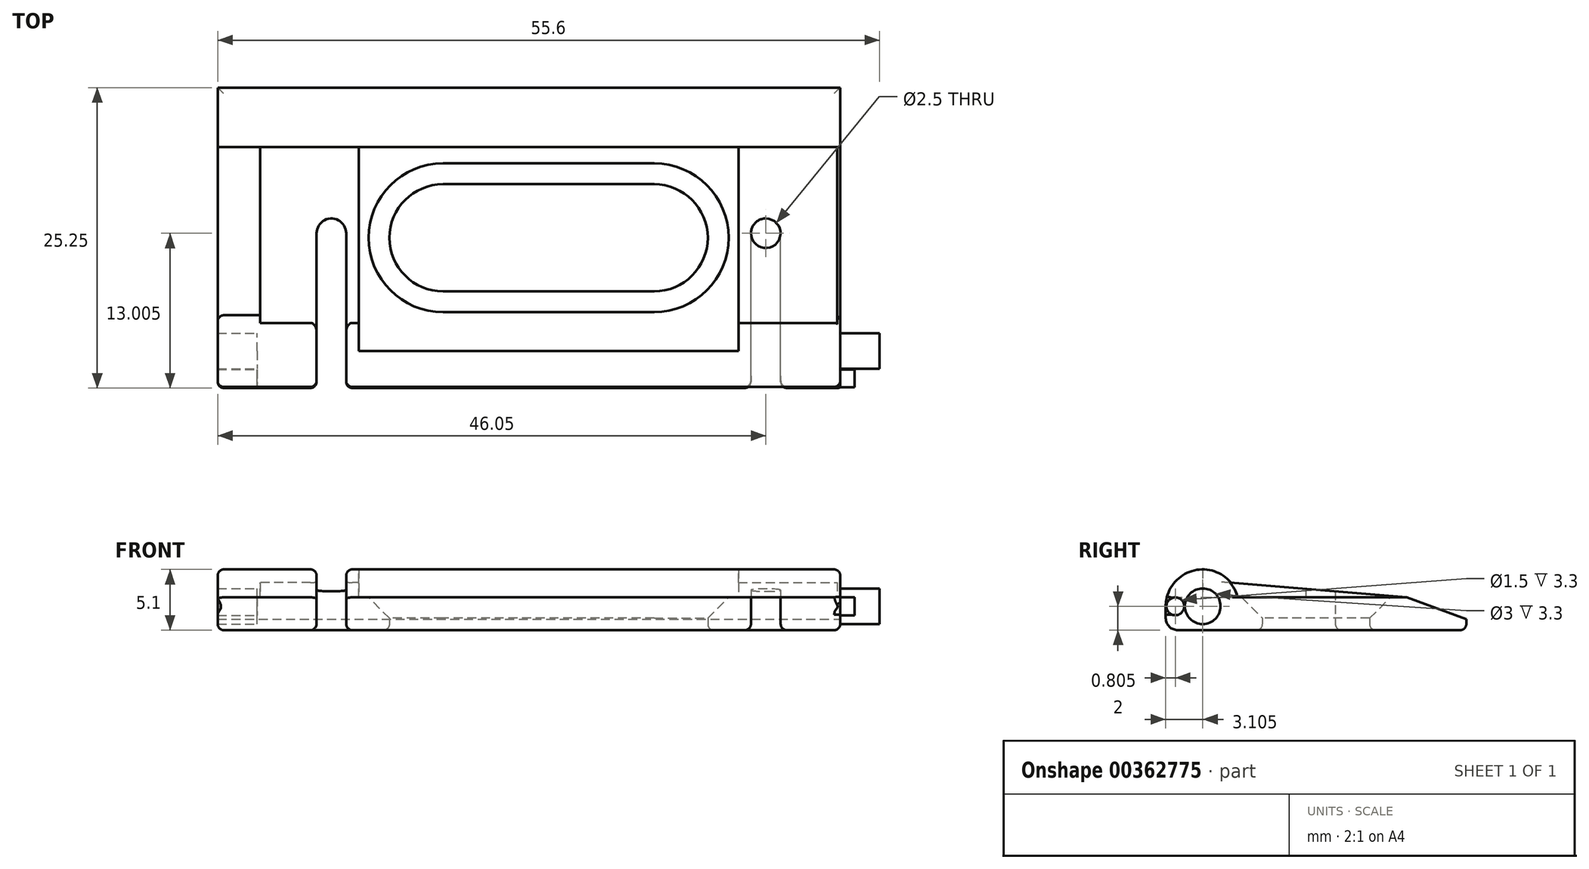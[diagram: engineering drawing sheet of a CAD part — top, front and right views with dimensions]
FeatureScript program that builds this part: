
annotation { "Feature Type Name" : "Feature", "Feature Type Description" : "" }
export const myFeature = defineFeature(function(context is Context, id is Id, definition is map)
    precondition{}
    {
        {
            var Q0;
            Q0=qCreatedBy(makeId("Top.planeOp"),FACE);
            var sketch = newSketch(context, id + "F0", { "sketchPlane" : qUnion([Q0])});
            skLineSegment(sketch, "E0.bottom", {"start": v(24.5, -12.62) * mm, "end": v(-24.5, -12.63) * mm});
            skLineSegment(sketch, "E0.top", {"start": v(24.5, 12.63) * mm, "end": v(-24.5, 12.62) * mm});
            skLineSegment(sketch, "E0.left", {"start": v(24.5, -12.62) * mm, "end": v(24.5, 12.63) * mm});
            skLineSegment(sketch, "E0.right", {"start": v(-24.5, -12.62) * mm, "end": v(-24.5, 12.62) * mm});
            skPoint(sketch, "E0.middle", {"position": v(0, 0) * mm});
            skLineSegment(sketch, "E1.bottom", {"start": v(8.88, -4.5) * mm, "end": v(-8.88, -4.5) * mm});
            skLineSegment(sketch, "E1.top", {"start": v(8.88, 4.5) * mm, "end": v(-8.88, 4.5) * mm});
            skLineSegment(sketch, "E1.left", {"start": v(8.88, -4.5) * mm, "end": v(8.88, 4.5) * mm});
            skLineSegment(sketch, "E1.right", {"start": v(-8.88, -4.5) * mm, "end": v(-8.88, 4.5) * mm});
            skCircle(sketch, "E2", {"center": v(-8.88, 0) * mm, "radius": 4.5 * mm});
            skCircle(sketch, "E3", {"center": v(8.88, 0) * mm, "radius": 4.5 * mm});
            skLineSegment(sketch, "E4", {"start": v(24.5, -12.62) * mm, "end": v(19.5, -12.62) * mm, "construction": true});
            skLineSegment(sketch, "E5.bottom", {"start": v(19.5, -12.62) * mm, "end": v(17, -12.62) * mm});
            skLineSegment(sketch, "E5.top", {"start": v(19.5, 0.38) * mm, "end": v(17, 0.38) * mm});
            skLineSegment(sketch, "E5.left", {"start": v(19.5, -12.62) * mm, "end": v(19.5, 0.38) * mm});
            skLineSegment(sketch, "E5.right", {"start": v(17, -12.62) * mm, "end": v(17, 0.38) * mm});
            skLineSegment(sketch, "E6.MirrorCS", {"start": v(-19.5, -12.62) * mm, "end": v(-19.5, 0.38) * mm});
            skLineSegment(sketch, "E7.MirrorCS", {"start": v(-17, -12.62) * mm, "end": v(-17, 0.38) * mm});
            skLineSegment(sketch, "E8.MirrorCS", {"start": v(-19.5, 0.38) * mm, "end": v(-17, 0.38) * mm});
            skLineSegment(sketch, "E9.MirrorCS", {"start": v(-19.5, -12.62) * mm, "end": v(-17, -12.62) * mm});
            skCircle(sketch, "E10", {"center": v(18.25, 0.38) * mm, "radius": 1.25 * mm});
            skCircle(sketch, "E11", {"center": v(-18.25, 0.38) * mm, "radius": 1.25 * mm});
            skSolve(sketch);
        }
        {
            var Q0;
            Q0=makeQuery(id+"F0.imprint","IMPRINT",FACE,{"disambiguationData":[TD([[makeQuery(id+"F0.imprint","IMPRINT",EDGE,{"derivedFrom":sQuery(id+"F0.wireOp",EDGE,"E0.bottom")}),-1.0]])]});
            extrude(context, id + "F1", {"entities" : qUnion([Q0]), "depth" : 2.75 * mm});
        }
        {
            var Q0;
            Q0=makeQuery(id+"F1.opExtrude","CAP_EDGE",EDGE,{"disambiguationData":[OSD([sQuery(id+"F0.wireOp",EDGE,"E2")])],"isStart":false});
            var Q1;
            Q1=makeQuery(id+"F1.opExtrude","CAP_EDGE",EDGE,{"disambiguationData":[OSD([sQuery(id+"F0.wireOp",EDGE,"E1.top")])],"isStart":false});
            var Q2;
            Q2=makeQuery(id+"F1.opExtrude","CAP_EDGE",EDGE,{"disambiguationData":[OSD([sQuery(id+"F0.wireOp",EDGE,"E3")])],"isStart":false});
            var Q3;
            Q3=makeQuery(id+"F1.opExtrude","CAP_EDGE",EDGE,{"disambiguationData":[OSD([sQuery(id+"F0.wireOp",EDGE,"E1.bottom")])],"isStart":false});
            chamfer(context, id + "F2", {"entities" : qUnion([Q0, Q1, Q2, Q3]), "width" : 1.75 * mm, "tangentPropagation" : true});
        }
        {
            var Q0;
            Q0=makeQuery(id+"F1.opExtrude","CAP_EDGE",EDGE,{"disambiguationData":[OSD([sQuery(id+"F0.wireOp",EDGE,"E1.bottom")])],"isStart":true});
            var Q1;
            Q1=makeQuery(id+"F1.opExtrude","CAP_EDGE",EDGE,{"disambiguationData":[OSD([sQuery(id+"F0.wireOp",EDGE,"E3")])],"isStart":true});
            var Q2;
            Q2=makeQuery(id+"F1.opExtrude","CAP_EDGE",EDGE,{"disambiguationData":[OSD([sQuery(id+"F0.wireOp",EDGE,"E1.top")])],"isStart":true});
            var Q3;
            Q3=makeQuery(id+"F1.opExtrude","CAP_EDGE",EDGE,{"disambiguationData":[OSD([sQuery(id+"F0.wireOp",EDGE,"E2")])],"isStart":true});
            fillet(context, id + "F3", {"entities" : qUnion([Q0, Q1, Q2, Q3]), "radius" : 0.5 * mm, "tangentPropagation" : true, "allowEdgeOverflow" : false});
        }
        {
            var Q0;
            Q0=makeQuery(id+"F1.opExtrude","CAP_EDGE",EDGE,{"disambiguationData":[OSD([sQuery(id+"F0.wireOp",EDGE,"E0.top")])],"isStart":false});
            chamfer(context, id + "F4", {"entities" : qUnion([Q0]), "chamferType" : ChamferType.OFFSET_ANGLE, "width" : 5 * mm, "oppositeDirection" : false, "angle" : 20 * degree, "tangentPropagation" : true});
        }
        {
            var Q0;
            Q0=makeQuery(id+"F1.opExtrude","SWEPT_FACE",FACE,{"disambiguationData":[OSD([sQuery(id+"F0.wireOp",EDGE,"E0.left")])]});
            var sketch = newSketch(context, id + "F5", { "sketchPlane" : qUnion([Q0])});
            skLineSegment(sketch, "E12.bottom", {"start": v(-12.62, 0) * mm, "end": v(-9.53, 0) * mm, "construction": true});
            skLineSegment(sketch, "E12.top", {"start": v(-12.62, 2) * mm, "end": v(-9.53, 2) * mm, "construction": true});
            skLineSegment(sketch, "E12.left", {"start": v(-12.62, 0) * mm, "end": v(-12.62, 2) * mm, "construction": true});
            skLineSegment(sketch, "E12.right", {"start": v(-9.53, 0) * mm, "end": v(-9.53, 2) * mm, "construction": true});
            skCircle(sketch, "E13", {"center": v(-9.53, 2) * mm, "radius": 3.1 * mm});
            skPoint(sketch, "E14", {"position": v(-7.16, 4) * mm});
            skLineSegment(sketch, "E15", {"start": v(-7.16, 4) * mm, "end": v(7.63, 2.75) * mm});
            skCircle(sketch, "E16", {"center": v(-9.53, 2) * mm, "radius": 1.5 * mm});
            skCircle(sketch, "E17", {"center": v(-11.83, 2) * mm, "radius": 0.75 * mm});
            skSolve(sketch);
        }
        {
            var Q0;
            {var subQ0=sQuery(id+"F5.wireOp",EDGE,"E13");var subQ1=makeQuery(id+"F1.opExtrude","CAP_EDGE",EDGE,{"disambiguationData":[OSD([sQuery(id+"F0.wireOp",EDGE,"E0.left")])],"isStart":false});var subQ2=makeQuery(id+"F5.imprint","INTERSECT",VERTEX,{"disambiguationData":[OD(0.0)],"derivedFrom":[subQ1,subQ0]});Q0=makeQuery(id+"F5.imprint","IMPRINT",FACE,{"disambiguationData":[TD([[makeQuery(id+"F5.imprint","IMPRINT",EDGE,{"disambiguationData":[TD([[subQ2,1.0]])],"derivedFrom":subQ0}),1.0]])]});}
            var Q1;
            {var subQ0=sQuery(id+"F5.wireOp",EDGE,"E16");var subQ1=makeQuery(id+"F1.opExtrude","CAP_EDGE",EDGE,{"disambiguationData":[OSD([sQuery(id+"F0.wireOp",EDGE,"E0.left")])],"isStart":false});var subQ2=makeQuery(id+"F5.imprint","INTERSECT",VERTEX,{"disambiguationData":[OD(0.0)],"derivedFrom":[subQ1,subQ0]});Q1=makeQuery(id+"F5.imprint","IMPRINT",FACE,{"disambiguationData":[TD([[makeQuery(id+"F5.imprint","IMPRINT",EDGE,{"disambiguationData":[TD([[subQ2,1.0]])],"derivedFrom":subQ0}),1.0]])]});}
            var Q2;
            Q2=makeQuery(id+"F1.opExtrude","SWEPT_FACE",FACE,{"disambiguationData":[OSD([sQuery(id+"F0.wireOp",EDGE,"E0.right")])]});
            extrude(context, id + "F6", {"entities" : qUnion([Q0, Q1]), "operationType" : NewBodyOperationType.ADD, "endBound" : BoundingType.UP_TO_SURFACE, "oppositeDirection" : true, "endBoundEntityFace" : qUnion([Q2]), "depth" : 25 * mm});
        }
        {
            var Q0;
            {var subQ0=sQuery(id+"F0.wireOp",EDGE,"E0.bottom");Q0=makeQuery(id+"F1.opExtrude","CAP_EDGE",EDGE,{"disambiguationData":[OSD([subQ0]),TDD([makeQuery(id+"F0.imprint","IMPRINT",EDGE,{"disambiguationData":[TD([[makeQuery(id+"F0.imprint","INTERSECT",VERTEX,{"derivedFrom":[subQ0,sQuery(id+"F0.wireOp",EDGE,"E0.left")]}),-1.0]])],"derivedFrom":subQ0})])],"isStart":false});}
            var Q1;
            {var subQ0=sQuery(id+"F0.wireOp",EDGE,"E0.bottom");Q1=makeQuery(id+"F1.opExtrude","CAP_EDGE",EDGE,{"disambiguationData":[OSD([subQ0]),TDD([makeQuery(id+"F0.imprint","IMPRINT",EDGE,{"disambiguationData":[TD([[makeQuery(id+"F0.imprint","INTERSECT",VERTEX,{"derivedFrom":[subQ0,sQuery(id+"F0.wireOp",EDGE,"E5.bottom"),sQuery(id+"F0.wireOp",EDGE,"E5.right")]}),-1.0]])],"derivedFrom":subQ0})])],"isStart":false});}
            var Q2;
            {var subQ0=sQuery(id+"F0.wireOp",EDGE,"E0.bottom");Q2=makeQuery(id+"F1.opExtrude","CAP_EDGE",EDGE,{"disambiguationData":[OSD([subQ0]),TDD([makeQuery(id+"F0.imprint","IMPRINT",EDGE,{"disambiguationData":[TD([[makeQuery(id+"F0.imprint","INTERSECT",VERTEX,{"derivedFrom":[subQ0,sQuery(id+"F0.wireOp",EDGE,"E0.right")]}),1.0]])],"derivedFrom":subQ0})])],"isStart":false});}
            fillet(context, id + "F7", {"entities" : qUnion([Q0, Q1, Q2]), "radius" : 2 * mm, "tangentPropagation" : true, "allowEdgeOverflow" : false});
        }
        {
            var Q0;
            {var subQ0=sQuery(id+"F0.wireOp",EDGE,"E0.bottom");Q0=makeQuery(id+"F1.opExtrude","CAP_EDGE",EDGE,{"disambiguationData":[OSD([subQ0]),TDD([makeQuery(id+"F0.imprint","IMPRINT",EDGE,{"disambiguationData":[TD([[makeQuery(id+"F0.imprint","INTERSECT",VERTEX,{"derivedFrom":[subQ0,sQuery(id+"F0.wireOp",EDGE,"E0.right")]}),1.0]])],"derivedFrom":subQ0})])],"isStart":true});}
            var Q1;
            {var subQ0=sQuery(id+"F0.wireOp",EDGE,"E0.bottom");Q1=makeQuery(id+"F1.opExtrude","CAP_EDGE",EDGE,{"disambiguationData":[OSD([subQ0]),TDD([makeQuery(id+"F0.imprint","IMPRINT",EDGE,{"disambiguationData":[TD([[makeQuery(id+"F0.imprint","INTERSECT",VERTEX,{"derivedFrom":[subQ0,sQuery(id+"F0.wireOp",EDGE,"E5.bottom"),sQuery(id+"F0.wireOp",EDGE,"E5.right")]}),-1.0]])],"derivedFrom":subQ0})])],"isStart":true});}
            var Q2;
            {var subQ0=sQuery(id+"F0.wireOp",EDGE,"E0.bottom");Q2=makeQuery(id+"F1.opExtrude","CAP_EDGE",EDGE,{"disambiguationData":[OSD([subQ0]),TDD([makeQuery(id+"F0.imprint","IMPRINT",EDGE,{"disambiguationData":[TD([[makeQuery(id+"F0.imprint","INTERSECT",VERTEX,{"derivedFrom":[subQ0,sQuery(id+"F0.wireOp",EDGE,"E0.left")]}),-1.0]])],"derivedFrom":subQ0})])],"isStart":true});}
            fillet(context, id + "F8", {"entities" : qUnion([Q0, Q1, Q2]), "radius" : 1 * mm, "tangentPropagation" : true, "allowEdgeOverflow" : false});
        }
        {
            var Q0;
            {var subQ0=sQuery(id+"F5.wireOp",EDGE,"E15");Q0=makeQuery(id+"F5.imprint","IMPRINT",FACE,{"disambiguationData":[TD([[makeQuery(id+"F5.imprint","IMPRINT",EDGE,{"derivedFrom":subQ0}),-1.0]])]});}
            extrude(context, id + "F9", {"entities" : qUnion([Q0]), "operationType" : NewBodyOperationType.ADD, "oppositeDirection" : true, "depth" : 8.55 * mm});
        }
        {
            var Q0;
            {var subQ0=sQuery(id+"F5.wireOp",EDGE,"E15");Q0=makeQuery(id+"F5.imprint","IMPRINT",FACE,{"disambiguationData":[TD([[makeQuery(id+"F5.imprint","IMPRINT",EDGE,{"derivedFrom":subQ0}),-1.0]])]});}
            extrude(context, id + "F10", {"entities" : qUnion([Q0]), "operationType" : NewBodyOperationType.REMOVE, "oppositeDirection" : true, "depth" : 0.25 * mm});
        }
        {
            var Q0;
            {var subQ0=sQuery(id+"F0.wireOp",EDGE,"E0.right");Q0=makeQuery(id+"F6.boolean.opBoolean","MERGE",FACE,{"derivedFrom":[makeQuery(id+"F1.opExtrude","SWEPT_FACE",FACE,{"disambiguationData":[OSD([subQ0])]}),makeQuery(id+"F6.opExtrude","CAP_FACE",FACE,{"disambiguationData":[OSD([subQ0])],"isStart":false})]});}
            var sketch = newSketch(context, id + "F11", { "sketchPlane" : qUnion([Q0])});
            skArc(sketch, "E18.0.0", {"start": v(7.16, 4) * mm, "mid": v(6.77, 3.41) * mm, "end": v(6.52, 2.75) * mm});
            skLineSegment(sketch, "E18.0.1", {"start": v(6.52, 2.75) * mm, "end": v(-7.63, 2.75) * mm});
            skLineSegment(sketch, "E18.0.2", {"start": v(-7.63, 2.75) * mm, "end": v(7.16, 4) * mm});
            skSolve(sketch);
        }
        {
            var Q0;
            Q0=makeQuery(id+"F11.imprint","IMPRINT",FACE,{"disambiguationData":[TD([[makeQuery(id+"F11.imprint","IMPRINT",EDGE,{"derivedFrom":sQuery(id+"F11.wireOp",EDGE,"E18.0.0")}),1.0]])]});
            extrude(context, id + "F12", {"entities" : qUnion([Q0]), "operationType" : NewBodyOperationType.ADD, "oppositeDirection" : true, "depth" : 8.55 * mm});
        }
        {
            var Q0;
            Q0=makeQuery(id+"F11.imprint","IMPRINT",FACE,{"disambiguationData":[TD([[makeQuery(id+"F11.imprint","IMPRINT",EDGE,{"derivedFrom":sQuery(id+"F11.wireOp",EDGE,"E18.0.0")}),1.0]])]});
            extrude(context, id + "F13", {"entities" : qUnion([Q0]), "operationType" : NewBodyOperationType.REMOVE, "oppositeDirection" : true, "depth" : 0.25 * mm});
        }
        {
            var Q0;
            {var subQ0=sQuery(id+"F0.wireOp",EDGE,"E6.MirrorCS");Q0=makeQuery(id+"F0.imprint","IMPRINT",FACE,{"disambiguationData":[TD([[makeQuery(id+"F0.imprint","IMPRINT",EDGE,{"derivedFrom":subQ0}),-1.0]])]});}
            var Q1;
            Q1=makeQuery(id+"F0.imprint","IMPRINT",FACE,{"disambiguationData":[TD([[makeQuery(id+"F0.imprint","IMPRINT",EDGE,{"derivedFrom":sQuery(id+"F0.wireOp",EDGE,"E5.bottom")}),-1.0]])]});
            var Q2;
            {var subQ0=sQuery(id+"F0.wireOp",EDGE,"E5.top");Q2=makeQuery(id+"F0.imprint","IMPRINT",FACE,{"disambiguationData":[TD([[makeQuery(id+"F0.imprint","IMPRINT",EDGE,{"derivedFrom":subQ0}),-1.0]])]});}
            var Q3;
            {var subQ0=sQuery(id+"F0.wireOp",EDGE,"E5.top");Q3=makeQuery(id+"F0.imprint","IMPRINT",FACE,{"disambiguationData":[TD([[makeQuery(id+"F0.imprint","IMPRINT",EDGE,{"derivedFrom":subQ0}),1.0]])]});}
            var Q4;
            {var subQ0=sQuery(id+"F0.wireOp",EDGE,"E8.MirrorCS");Q4=makeQuery(id+"F0.imprint","IMPRINT",FACE,{"disambiguationData":[TD([[makeQuery(id+"F0.imprint","IMPRINT",EDGE,{"derivedFrom":subQ0}),-1.0]])]});}
            var Q5;
            {var subQ0=sQuery(id+"F0.wireOp",EDGE,"E8.MirrorCS");Q5=makeQuery(id+"F0.imprint","IMPRINT",FACE,{"disambiguationData":[TD([[makeQuery(id+"F0.imprint","IMPRINT",EDGE,{"derivedFrom":subQ0}),1.0]])]});}
            extrude(context, id + "F14", {"entities" : qUnion([Q0, Q1, Q2, Q3, Q4, Q5]), "operationType" : NewBodyOperationType.REMOVE, "depth" : 6 * mm});
        }
        {
            var Q0;
            {var subQ0=sQuery(id+"F0.wireOp",EDGE,"E1.top");var subQ2=sQuery(id+"F0.wireOp",EDGE,"E0.left");var subQ3=sQuery(id+"F0.wireOp",EDGE,"E10");var subQ4=sQuery(id+"F0.wireOp",EDGE,"E1.bottom");var subQ5=sQuery(id+"F0.wireOp",EDGE,"E7.MirrorCS");var subQ6=sQuery(id+"F0.wireOp",EDGE,"E6.MirrorCS");var subQ7=sQuery(id+"F0.wireOp",EDGE,"E11");var subQ8=sQuery(id+"F0.wireOp",EDGE,"E0.right");var subQ9=sQuery(id+"F0.wireOp",EDGE,"E5.left");var subQ10=sQuery(id+"F0.wireOp",EDGE,"E3");var subQ11=sQuery(id+"F0.wireOp",EDGE,"E5.right");var subQ12=sQuery(id+"F0.wireOp",EDGE,"E2");var subQ13=sQuery(id+"F0.wireOp",EDGE,"E0.top");Q0=makeQuery(id+"F6.boolean.opBoolean","SPLIT",FACE,{"disambiguationData":[TD([makeQuery(id+"F1.opExtrude","SWEPT_FACE",FACE,{"disambiguationData":[OSD([subQ3])]})])],"derivedFrom":makeQuery(id+"F1.opExtrude","CAP_FACE",FACE,{"disambiguationData":[OSD([sQuery(id+"F0.wireOp",EDGE,"E0.bottom"),subQ13,subQ2,subQ8,subQ4,subQ0,subQ12,subQ10,subQ9,subQ11,subQ6,subQ5,subQ3,subQ7])],"isStart":false})});}
            var sketch = newSketch(context, id + "F15", { "sketchPlane" : qUnion([Q0])});
            skLineSegment(sketch, "E19.0", {"start": v(15.95, -7.16) * mm, "end": v(15.95, 7.63) * mm, "construction": true});
            skLineSegment(sketch, "E20.0", {"start": v(-15.95, 7.63) * mm, "end": v(-15.95, -7.16) * mm, "construction": true});
            skLineSegment(sketch, "E21.0", {"start": v(-17, -12.53) * mm, "end": v(17, -12.53) * mm, "construction": true});
            skLineSegment(sketch, "E21.1", {"start": v(-15.95, -6.52) * mm, "end": v(15.95, -6.52) * mm, "construction": true});
            skLineSegment(sketch, "E22", {"start": v(15.95, -6.52) * mm, "end": v(15.95, -12.53) * mm});
            skLineSegment(sketch, "E23", {"start": v(-15.95, -6.52) * mm, "end": v(-15.95, -12.53) * mm});
            skPoint(sketch, "E24", {"position": v(15.95, -9.52) * mm});
            skPoint(sketch, "E25", {"position": v(-15.95, -9.53) * mm});
            skLineSegment(sketch, "E26", {"start": v(15.95, -9.52) * mm, "end": v(-15.95, -9.53) * mm});
            skLineSegment(sketch, "E27", {"start": v(-15.95, -6.52) * mm, "end": v(15.95, -6.52) * mm});
            skSolve(sketch);
        }
        {
            var Q0;
            {var subQ2=sQuery(id+"F15.wireOp",EDGE,"E26");Q0=makeQuery(id+"F15.imprint","IMPRINT",FACE,{"disambiguationData":[TD([[makeQuery(id+"F15.imprint","IMPRINT",EDGE,{"derivedFrom":subQ2}),-1.0]])]});}
            extrude(context, id + "F16", {"entities" : qUnion([Q0]), "operationType" : NewBodyOperationType.REMOVE, "depth" : 5 * mm});
        }
        {
            var Q0;
            Q0=makeQuery(id+"F5.imprint","IMPRINT",FACE,{"disambiguationData":[TD([[makeQuery(id+"F5.imprint","IMPRINT",EDGE,{"derivedFrom":sQuery(id+"F5.wireOp",EDGE,"E17")}),1.0]])]});
            extrude(context, id + "F17", {"entities" : qUnion([Q0]), "operationType" : NewBodyOperationType.ADD, "depth" : 1.2 * mm});
        }
        {
            var Q0;
            {var subQ0=sQuery(id+"F5.wireOp",EDGE,"E16");var subQ1=makeQuery(id+"F1.opExtrude","CAP_EDGE",EDGE,{"disambiguationData":[OSD([sQuery(id+"F0.wireOp",EDGE,"E0.left")])],"isStart":false});var subQ2=makeQuery(id+"F5.imprint","INTERSECT",VERTEX,{"disambiguationData":[OD(0.0)],"derivedFrom":[subQ1,subQ0]});Q0=makeQuery(id+"F5.imprint","IMPRINT",FACE,{"disambiguationData":[TD([[makeQuery(id+"F5.imprint","IMPRINT",EDGE,{"disambiguationData":[TD([[subQ2,1.0]])],"derivedFrom":subQ0}),1.0]])]});}
            var Q1;
            {var subQ0=sQuery(id+"F5.wireOp",EDGE,"E16");var subQ1=makeQuery(id+"F1.opExtrude","CAP_EDGE",EDGE,{"disambiguationData":[OSD([sQuery(id+"F0.wireOp",EDGE,"E0.left")])],"isStart":false});var subQ2=makeQuery(id+"F5.imprint","INTERSECT",VERTEX,{"disambiguationData":[OD(0.0)],"derivedFrom":[subQ1,subQ0]});Q1=makeQuery(id+"F5.imprint","IMPRINT",FACE,{"disambiguationData":[TD([[makeQuery(id+"F5.imprint","IMPRINT",EDGE,{"disambiguationData":[TD([[subQ2,-1.0]])],"derivedFrom":subQ0}),1.0]])]});}
            var Q2;
            Q2=sQuery(id+"F5.wireOp",EDGE,"E16");
            extrude(context, id + "F18", {"entities" : qUnion([Q0, Q1]), "operationType" : NewBodyOperationType.ADD, "surfaceEntities" : qUnion([Q2]), "depth" : 3.3 * mm});
        }
        {
            var Q0;
            {var subQ3=sQuery(id+"F11.wireOp",EDGE,"E18.0.0");Q0=makeQuery(id+"F11.imprint","IMPRINT",FACE,{"disambiguationData":[TD([[makeQuery(id+"F11.imprint","IMPRINT",EDGE,{"derivedFrom":subQ3}),-1.0]])]});}
            var sketch = newSketch(context, id + "F19", { "sketchPlane" : qUnion([Q0])});
            skCircle(sketch, "E28.0", {"center": v(9.52, 2) * mm, "radius": 1.5 * mm});
            skCircle(sketch, "E29.0", {"center": v(11.82, 2) * mm, "radius": 0.75 * mm});
            skSolve(sketch);
        }
        {
            var Q0;
            Q0=makeQuery(id+"F19.imprint","IMPRINT",FACE,{"disambiguationData":[TD([[makeQuery(id+"F19.imprint","IMPRINT",EDGE,{"derivedFrom":sQuery(id+"F19.wireOp",EDGE,"E28.0")}),-1.0]])]});
            extrude(context, id + "F20", {"entities" : qUnion([Q0]), "operationType" : NewBodyOperationType.ADD, "depth" : 3.3 * mm});
        }
        {
            var Q0;
            Q0=makeQuery(id+"F19.imprint","IMPRINT",FACE,{"disambiguationData":[TD([[makeQuery(id+"F19.imprint","IMPRINT",EDGE,{"derivedFrom":sQuery(id+"F19.wireOp",EDGE,"E29.0")}),-1.0]])]});
            var Q1;
            Q1=sQuery(id+"F19.wireOp",EDGE,"E29.0");
            extrude(context, id + "F21", {"entities" : qUnion([Q0]), "operationType" : NewBodyOperationType.ADD, "surfaceEntities" : qUnion([Q1]), "depth" : 1.2 * mm});
        }
        {
            var Q0;
            Q0=makeQuery(id+"F1.opExtrude","CAP_FACE",FACE,{"disambiguationData":[OSD([sQuery(id+"F0.wireOp",EDGE,"E0.bottom"),sQuery(id+"F0.wireOp",EDGE,"E0.top"),sQuery(id+"F0.wireOp",EDGE,"E0.left"),sQuery(id+"F0.wireOp",EDGE,"E0.right"),sQuery(id+"F0.wireOp",EDGE,"E1.bottom"),sQuery(id+"F0.wireOp",EDGE,"E1.top"),sQuery(id+"F0.wireOp",EDGE,"E2"),sQuery(id+"F0.wireOp",EDGE,"E3"),sQuery(id+"F0.wireOp",EDGE,"E5.left"),sQuery(id+"F0.wireOp",EDGE,"E5.right"),sQuery(id+"F0.wireOp",EDGE,"E6.MirrorCS"),sQuery(id+"F0.wireOp",EDGE,"E7.MirrorCS"),sQuery(id+"F0.wireOp",EDGE,"E10"),sQuery(id+"F0.wireOp",EDGE,"E11")])],"isStart":true});
            fillet(context, id + "F22", {"entities" : qUnion([Q0]), "radius" : 0.5 * mm, "tangentPropagation" : true, "allowEdgeOverflow" : false});
        }
    });
